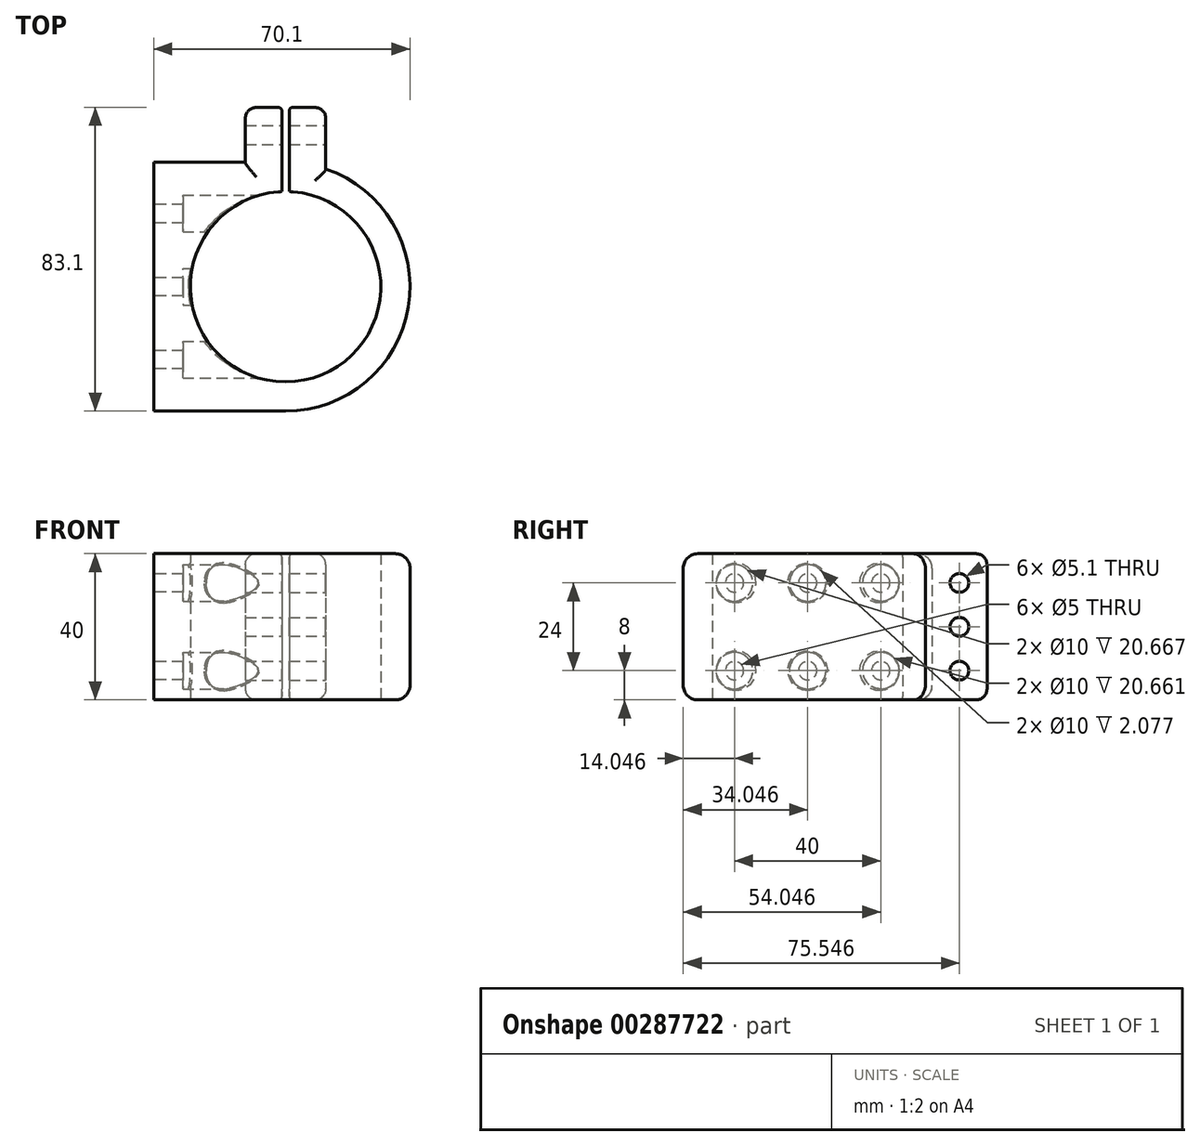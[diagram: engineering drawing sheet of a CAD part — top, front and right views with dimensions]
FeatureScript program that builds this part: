
annotation { "Feature Type Name" : "Feature", "Feature Type Description" : "" }
export const myFeature = defineFeature(function(context is Context, id is Id, definition is map)
    precondition{}
    {
        {
            var Q0;
            Q0=qCreatedBy(makeId("Top.planeOp"),FACE);
            var sketch = newSketch(context, id + "F0", { "sketchPlane" : qUnion([Q0])});
            skLineSegment(sketch, "E0.bottom", {"start": v(-43.2, -23.77) * mm, "end": v(-7.15, -23.77) * mm, "construction": true});
            skLineSegment(sketch, "E0.top", {"start": v(-43.2, 28.33) * mm, "end": v(-7.15, 28.33) * mm, "construction": true});
            skLineSegment(sketch, "E0.left", {"start": v(-43.2, -23.77) * mm, "end": v(-43.2, 28.33) * mm});
            skLineSegment(sketch, "E0.right", {"start": v(-7.15, -23.77) * mm, "end": v(-7.15, 28.33) * mm, "construction": true});
            skArc(sketch, "E1", {"start": v(-7.15, -23.77) * mm, "mid": v(18.9, 2.28) * mm, "end": v(-7.15, 28.33) * mm});
            skLineSegment(sketch, "E2", {"start": v(-43.2, -23.77) * mm, "end": v(-43.2, -31.77) * mm});
            skLineSegment(sketch, "E3", {"start": v(-43.2, -31.77) * mm, "end": v(-7.15, -31.77) * mm});
            skLineSegment(sketch, "E4", {"start": v(-43.2, 28.33) * mm, "end": v(-43.2, 36.33) * mm});
            skLineSegment(sketch, "E5", {"start": v(-43.2, 36.33) * mm, "end": v(-7.15, 36.33) * mm});
            skArc(sketch, "E6", {"start": v(-7.15, -31.77) * mm, "mid": v(26.9, 2.28) * mm, "end": v(-7.15, 36.33) * mm});
            skCircle(sketch, "E7", {"center": v(-7.15, 2.28) * mm, "radius": 26.05 * mm});
            skLineSegment(sketch, "E8", {"start": v(-18.15, 36.33) * mm, "end": v(-18.15, 51.33) * mm});
            skLineSegment(sketch, "E9", {"start": v(-8.15, 36.33) * mm, "end": v(-8.15, 51.33) * mm});
            skLineSegment(sketch, "E10", {"start": v(-8.15, 51.33) * mm, "end": v(-18.15, 51.33) * mm});
            skLineSegment(sketch, "E11", {"start": v(-6.15, 36.31) * mm, "end": v(-6.15, 51.33) * mm});
            skLineSegment(sketch, "E12", {"start": v(-6.15, 51.33) * mm, "end": v(3.85, 51.33) * mm});
            skLineSegment(sketch, "E13", {"start": v(3.85, 51.33) * mm, "end": v(3.85, 34.5) * mm});
            skLineSegment(sketch, "E14", {"start": v(-8.15, 36.33) * mm, "end": v(-8.15, 28.3) * mm});
            skLineSegment(sketch, "E15", {"start": v(-6.15, 36.31) * mm, "end": v(-6.15, 28.3) * mm});
            skSolve(sketch);
        }
        {
            var Q0;
            Q0=makeQuery(id+"F0.imprint","IMPRINT",FACE,{"disambiguationData":[TD([[makeQuery(id+"F0.imprint","IMPRINT",EDGE,{"derivedFrom":sQuery(id+"F0.wireOp",EDGE,"E0.left")}),-1.0]])]});
            var Q1;
            {var subQ0=sQuery(id+"F0.wireOp",EDGE,"E11");Q1=makeQuery(id+"F0.imprint","IMPRINT",FACE,{"disambiguationData":[TD([[makeQuery(id+"F0.imprint","IMPRINT",EDGE,{"derivedFrom":subQ0}),-1.0]])]});}
            var Q2;
            {var subQ0=sQuery(id+"F0.wireOp",EDGE,"E8");Q2=makeQuery(id+"F0.imprint","IMPRINT",FACE,{"disambiguationData":[TD([[makeQuery(id+"F0.imprint","IMPRINT",EDGE,{"derivedFrom":subQ0}),-1.0]])]});}
            extrude(context, id + "F1", {"entities" : qUnion([Q0, Q1, Q2]), "depth" : 40 * mm});
        }
        {
            var Q0;
            Q0=makeQuery(id+"F1.opExtrude","SWEPT_FACE",FACE,{"disambiguationData":[OSD([sQuery(id+"F0.wireOp",EDGE,"E13")])]});
            var sketch = newSketch(context, id + "F2", { "sketchPlane" : qUnion([Q0])});
            skCircle(sketch, "E16", {"center": v(43.78, 32) * mm, "radius": 2.55 * mm});
            skCircle(sketch, "E17", {"center": v(43.78, 20) * mm, "radius": 2.55 * mm});
            skCircle(sketch, "E18", {"center": v(43.78, 8) * mm, "radius": 2.55 * mm});
            skLineSegment(sketch, "E19", {"start": v(43.78, 32) * mm, "end": v(43.78, 20) * mm, "construction": true});
            skLineSegment(sketch, "E20", {"start": v(43.78, 20) * mm, "end": v(43.78, 8) * mm, "construction": true});
            skSolve(sketch);
        }
        {
            var Q0;
            Q0=makeQuery(id+"F2.imprint","IMPRINT",FACE,{"disambiguationData":[TD([[makeQuery(id+"F2.imprint","IMPRINT",EDGE,{"derivedFrom":sQuery(id+"F2.wireOp",EDGE,"E16")}),1.0]])]});
            var Q1;
            Q1=makeQuery(id+"F2.imprint","IMPRINT",FACE,{"disambiguationData":[TD([[makeQuery(id+"F2.imprint","IMPRINT",EDGE,{"derivedFrom":sQuery(id+"F2.wireOp",EDGE,"E17")}),1.0]])]});
            var Q2;
            Q2=makeQuery(id+"F2.imprint","IMPRINT",FACE,{"disambiguationData":[TD([[makeQuery(id+"F2.imprint","IMPRINT",EDGE,{"derivedFrom":sQuery(id+"F2.wireOp",EDGE,"E18")}),1.0]])]});
            extrude(context, id + "F3", {"entities" : qUnion([Q0, Q1, Q2]), "operationType" : NewBodyOperationType.REMOVE, "oppositeDirection" : true, "depth" : 25 * mm});
        }
        {
            var Q0;
            Q0=makeQuery(id+"F1.opExtrude","SWEPT_FACE",FACE,{"disambiguationData":[OSD([sQuery(id+"F0.wireOp",EDGE,"E0.left"),sQuery(id+"F0.wireOp",EDGE,"E2"),sQuery(id+"F0.wireOp",EDGE,"E4")])]});
            var sketch = newSketch(context, id + "F4", { "sketchPlane" : qUnion([Q0])});
            skCircle(sketch, "E21", {"center": v(-22.28, 32) * mm, "radius": 2.5 * mm});
            skCircle(sketch, "E22", {"center": v(17.72, 32) * mm, "radius": 2.5 * mm});
            skCircle(sketch, "E23", {"center": v(17.72, 8) * mm, "radius": 2.5 * mm});
            skCircle(sketch, "E24", {"center": v(-22.28, 8) * mm, "radius": 2.5 * mm});
            skLineSegment(sketch, "E25", {"start": v(-22.28, 32) * mm, "end": v(17.72, 32) * mm, "construction": true});
            skLineSegment(sketch, "E26", {"start": v(-2.28, 40) * mm, "end": v(-2.28, 32) * mm, "construction": true});
            skCircle(sketch, "E27", {"center": v(-2.28, 32) * mm, "radius": 2.5 * mm});
            skCircle(sketch, "E28", {"center": v(-2.28, 8) * mm, "radius": 2.5 * mm});
            skSolve(sketch);
        }
        {
            var Q0;
            Q0=makeQuery(id+"F4.imprint","IMPRINT",FACE,{"disambiguationData":[TD([[makeQuery(id+"F4.imprint","IMPRINT",EDGE,{"derivedFrom":sQuery(id+"F4.wireOp",EDGE,"E21")}),1.0]])]});
            var Q1;
            Q1=makeQuery(id+"F4.imprint","IMPRINT",FACE,{"disambiguationData":[TD([[makeQuery(id+"F4.imprint","IMPRINT",EDGE,{"derivedFrom":sQuery(id+"F4.wireOp",EDGE,"E22")}),1.0]])]});
            var Q2;
            Q2=makeQuery(id+"F4.imprint","IMPRINT",FACE,{"disambiguationData":[TD([[makeQuery(id+"F4.imprint","IMPRINT",EDGE,{"derivedFrom":sQuery(id+"F4.wireOp",EDGE,"E23")}),1.0]])]});
            var Q3;
            Q3=makeQuery(id+"F4.imprint","IMPRINT",FACE,{"disambiguationData":[TD([[makeQuery(id+"F4.imprint","IMPRINT",EDGE,{"derivedFrom":sQuery(id+"F4.wireOp",EDGE,"E24")}),1.0]])]});
            var Q4;
            Q4=makeQuery(id+"F4.imprint","IMPRINT",FACE,{"disambiguationData":[TD([[makeQuery(id+"F4.imprint","IMPRINT",EDGE,{"derivedFrom":sQuery(id+"F4.wireOp",EDGE,"E27")}),1.0]])]});
            var Q5;
            Q5=makeQuery(id+"F4.imprint","IMPRINT",FACE,{"disambiguationData":[TD([[makeQuery(id+"F4.imprint","IMPRINT",EDGE,{"derivedFrom":sQuery(id+"F4.wireOp",EDGE,"E28")}),1.0]])]});
            extrude(context, id + "F5", {"entities" : qUnion([Q0, Q1, Q2, Q3, Q4, Q5]), "operationType" : NewBodyOperationType.REMOVE, "oppositeDirection" : true, "depth" : 25 * mm});
        }
        {
            var Q0;
            Q0=makeQuery(id+"F1.opExtrude","SWEPT_FACE",FACE,{"disambiguationData":[OSD([sQuery(id+"F0.wireOp",EDGE,"E0.left"),sQuery(id+"F0.wireOp",EDGE,"E2"),sQuery(id+"F0.wireOp",EDGE,"E4")])]});
            cPlane(context, id + "F6", {"entities" : qUnion([Q0]), "cplaneType" : CPlaneType.OFFSET, "offset" : 30 * mm, "oppositeDirection" : true, "width" : 150 * mm, "height" : 150 * mm});
        }
        {
            var Q0;
            Q0=qCreatedBy(id+"F6.planeOp",FACE);
            var sketch = newSketch(context, id + "F7", { "sketchPlane" : qUnion([Q0])});
            skCircle(sketch, "E29.0", {"center": v(17.72, 32) * mm, "radius": 2.5 * mm});
            skCircle(sketch, "E30.0", {"center": v(-2.28, 32) * mm, "radius": 2.5 * mm});
            skCircle(sketch, "E31.0", {"center": v(-22.28, 32) * mm, "radius": 2.5 * mm});
            skCircle(sketch, "E32.0", {"center": v(-22.28, 8) * mm, "radius": 2.5 * mm});
            skCircle(sketch, "E33.0", {"center": v(-2.28, 8) * mm, "radius": 2.5 * mm});
            skCircle(sketch, "E34.0", {"center": v(17.72, 8) * mm, "radius": 2.5 * mm});
            skCircle(sketch, "E35", {"center": v(17.72, 32) * mm, "radius": 5 * mm});
            skCircle(sketch, "E36", {"center": v(-2.28, 32) * mm, "radius": 5 * mm});
            skCircle(sketch, "E37", {"center": v(-22.28, 32) * mm, "radius": 5 * mm});
            skCircle(sketch, "E38", {"center": v(-22.28, 8) * mm, "radius": 5 * mm});
            skCircle(sketch, "E39", {"center": v(-2.28, 8) * mm, "radius": 5 * mm});
            skCircle(sketch, "E40", {"center": v(17.72, 8) * mm, "radius": 5 * mm});
            skSolve(sketch);
        }
        {
            var Q0;
            Q0=makeQuery(id+"F7.imprint","IMPRINT",FACE,{"disambiguationData":[TD([[makeQuery(id+"F7.imprint","IMPRINT",EDGE,{"derivedFrom":sQuery(id+"F7.wireOp",EDGE,"E29.0")}),-1.0]])]});
            var Q1;
            Q1=makeQuery(id+"F7.imprint","IMPRINT",FACE,{"disambiguationData":[TD([[makeQuery(id+"F7.imprint","IMPRINT",EDGE,{"derivedFrom":sQuery(id+"F7.wireOp",EDGE,"E34.0")}),-1.0]])]});
            var Q2;
            Q2=makeQuery(id+"F7.imprint","IMPRINT",FACE,{"disambiguationData":[TD([[makeQuery(id+"F7.imprint","IMPRINT",EDGE,{"derivedFrom":sQuery(id+"F7.wireOp",EDGE,"E32.0")}),-1.0]])]});
            var Q3;
            Q3=makeQuery(id+"F7.imprint","IMPRINT",FACE,{"disambiguationData":[TD([[makeQuery(id+"F7.imprint","IMPRINT",EDGE,{"derivedFrom":sQuery(id+"F7.wireOp",EDGE,"E31.0")}),-1.0]])]});
            var Q4;
            Q4=makeQuery(id+"F7.imprint","IMPRINT",FACE,{"disambiguationData":[TD([[makeQuery(id+"F7.imprint","IMPRINT",EDGE,{"derivedFrom":sQuery(id+"F7.wireOp",EDGE,"E30.0")}),-1.0]])]});
            var Q5;
            Q5=makeQuery(id+"F7.imprint","IMPRINT",FACE,{"disambiguationData":[TD([[makeQuery(id+"F7.imprint","IMPRINT",EDGE,{"derivedFrom":sQuery(id+"F7.wireOp",EDGE,"E33.0")}),-1.0]])]});
            extrude(context, id + "F8", {"entities" : qUnion([Q0, Q1, Q2, Q3, Q4, Q5]), "operationType" : NewBodyOperationType.REMOVE, "depth" : 22 * mm});
        }
        {
            var Q0;
            Q0=makeQuery(id+"F1.opExtrude","CAP_EDGE",EDGE,{"disambiguationData":[OSD([sQuery(id+"F0.wireOp",EDGE,"E6")])],"isStart":false});
            var Q1;
            Q1=makeQuery(id+"F1.opExtrude","CAP_EDGE",EDGE,{"disambiguationData":[OSD([sQuery(id+"F0.wireOp",EDGE,"E6")])],"isStart":true});
            var Q2;
            Q2=makeQuery(id+"F1.opExtrude","CAP_EDGE",EDGE,{"disambiguationData":[OSD([sQuery(id+"F0.wireOp",EDGE,"E5")])],"isStart":true});
            var Q3;
            Q3=makeQuery(id+"F1.opExtrude","CAP_EDGE",EDGE,{"disambiguationData":[OSD([sQuery(id+"F0.wireOp",EDGE,"E5")])],"isStart":false});
            fillet(context, id + "F9", {"entities" : qUnion([Q0, Q1, Q2, Q3]), "radius" : 4 * mm, "tangentPropagation" : true, "allowEdgeOverflow" : false});
        }
        {
            var Q0;
            Q0=makeQuery(id+"F8.boolean.opBoolean","INTERSECT",EDGE,{"derivedFrom":[makeQuery(id+"F1.opExtrude","SWEPT_FACE",FACE,{"disambiguationData":[OSD([sQuery(id+"F0.wireOp",EDGE,"E7")])]}),makeQuery(id+"F8.opExtrude","SWEPT_FACE",FACE,{"disambiguationData":[OSD([sQuery(id+"F7.wireOp",EDGE,"E40")])]})]});
            var Q1;
            Q1=makeQuery(id+"F8.boolean.opBoolean","INTERSECT",EDGE,{"derivedFrom":[makeQuery(id+"F1.opExtrude","SWEPT_FACE",FACE,{"disambiguationData":[OSD([sQuery(id+"F0.wireOp",EDGE,"E7")])]}),makeQuery(id+"F8.opExtrude","SWEPT_FACE",FACE,{"disambiguationData":[OSD([sQuery(id+"F7.wireOp",EDGE,"E35")])]})]});
            var Q2;
            Q2=makeQuery(id+"F8.boolean.opBoolean","INTERSECT",EDGE,{"derivedFrom":[makeQuery(id+"F1.opExtrude","SWEPT_FACE",FACE,{"disambiguationData":[OSD([sQuery(id+"F0.wireOp",EDGE,"E7")])]}),makeQuery(id+"F8.opExtrude","SWEPT_FACE",FACE,{"disambiguationData":[OSD([sQuery(id+"F7.wireOp",EDGE,"E39")])]})]});
            var Q3;
            Q3=makeQuery(id+"F8.boolean.opBoolean","INTERSECT",EDGE,{"derivedFrom":[makeQuery(id+"F1.opExtrude","SWEPT_FACE",FACE,{"disambiguationData":[OSD([sQuery(id+"F0.wireOp",EDGE,"E7")])]}),makeQuery(id+"F8.opExtrude","SWEPT_FACE",FACE,{"disambiguationData":[OSD([sQuery(id+"F7.wireOp",EDGE,"E36")])]})]});
            var Q4;
            Q4=makeQuery(id+"F8.boolean.opBoolean","INTERSECT",EDGE,{"derivedFrom":[makeQuery(id+"F1.opExtrude","SWEPT_FACE",FACE,{"disambiguationData":[OSD([sQuery(id+"F0.wireOp",EDGE,"E7")])]}),makeQuery(id+"F8.opExtrude","SWEPT_FACE",FACE,{"disambiguationData":[OSD([sQuery(id+"F7.wireOp",EDGE,"E38")])]})]});
            var Q5;
            Q5=makeQuery(id+"F8.boolean.opBoolean","INTERSECT",EDGE,{"derivedFrom":[makeQuery(id+"F1.opExtrude","SWEPT_FACE",FACE,{"disambiguationData":[OSD([sQuery(id+"F0.wireOp",EDGE,"E7")])]}),makeQuery(id+"F8.opExtrude","SWEPT_FACE",FACE,{"disambiguationData":[OSD([sQuery(id+"F7.wireOp",EDGE,"E37")])]})]});
            fillet(context, id + "F10", {"entities" : qUnion([Q0, Q1, Q2, Q3, Q4, Q5]), "radius" : 0.5 * mm, "tangentPropagation" : true, "allowEdgeOverflow" : false});
        }
        {
            var Q0;
            Q0=makeQuery(id+"F1.opExtrude","CAP_EDGE",EDGE,{"disambiguationData":[OSD([sQuery(id+"F0.wireOp",EDGE,"E8")])],"isStart":true});
            var Q1;
            Q1=makeQuery(id+"F1.opExtrude","SWEPT_EDGE",EDGE,{"disambiguationData":[OSD([sQuery(id+"F0.wireOp",EDGE,"E8"),sQuery(id+"F0.wireOp",EDGE,"E10")])]});
            var Q2;
            Q2=makeQuery(id+"F1.opExtrude","CAP_EDGE",EDGE,{"disambiguationData":[OSD([sQuery(id+"F0.wireOp",EDGE,"E8")])],"isStart":false});
            var Q3;
            Q3=makeQuery(id+"F1.opExtrude","CAP_EDGE",EDGE,{"disambiguationData":[OSD([sQuery(id+"F0.wireOp",EDGE,"E10")])],"isStart":false});
            var Q4;
            Q4=makeQuery(id+"F1.opExtrude","CAP_EDGE",EDGE,{"disambiguationData":[OSD([sQuery(id+"F0.wireOp",EDGE,"E10")])],"isStart":true});
            var Q5;
            Q5=makeQuery(id+"F1.opExtrude","CAP_EDGE",EDGE,{"disambiguationData":[OSD([sQuery(id+"F0.wireOp",EDGE,"E12")])],"isStart":true});
            var Q6;
            Q6=makeQuery(id+"F1.opExtrude","CAP_EDGE",EDGE,{"disambiguationData":[OSD([sQuery(id+"F0.wireOp",EDGE,"E12")])],"isStart":false});
            var Q7;
            Q7=makeQuery(id+"F1.opExtrude","SWEPT_EDGE",EDGE,{"disambiguationData":[OSD([sQuery(id+"F0.wireOp",EDGE,"E12"),sQuery(id+"F0.wireOp",EDGE,"E13")])]});
            var Q8;
            Q8=makeQuery(id+"F1.opExtrude","CAP_EDGE",EDGE,{"disambiguationData":[OSD([sQuery(id+"F0.wireOp",EDGE,"E13")])],"isStart":true});
            var Q9;
            Q9=makeQuery(id+"F1.opExtrude","CAP_EDGE",EDGE,{"disambiguationData":[OSD([sQuery(id+"F0.wireOp",EDGE,"E13")])],"isStart":false});
            fillet(context, id + "F11", {"entities" : qUnion([Q0, Q1, Q2, Q3, Q4, Q5, Q6, Q7, Q8, Q9]), "radius" : 3 * mm, "tangentPropagation" : true, "allowEdgeOverflow" : false});
        }
        {
            var Q0;
            Q0=makeQuery(id+"F1.opExtrude","CAP_EDGE",EDGE,{"disambiguationData":[OSD([sQuery(id+"F0.wireOp",EDGE,"E9"),sQuery(id+"F0.wireOp",EDGE,"E14")])],"isStart":true});
            var Q1;
            Q1=makeQuery(id+"F1.opExtrude","CAP_EDGE",EDGE,{"disambiguationData":[OSD([sQuery(id+"F0.wireOp",EDGE,"E11"),sQuery(id+"F0.wireOp",EDGE,"E15")])],"isStart":true});
            var Q2;
            Q2=makeQuery(id+"F1.opExtrude","SWEPT_EDGE",EDGE,{"disambiguationData":[OSD([sQuery(id+"F0.wireOp",EDGE,"E11"),sQuery(id+"F0.wireOp",EDGE,"E12")])]});
            var Q3;
            Q3=makeQuery(id+"F1.opExtrude","SWEPT_EDGE",EDGE,{"disambiguationData":[OSD([sQuery(id+"F0.wireOp",EDGE,"E9"),sQuery(id+"F0.wireOp",EDGE,"E10")])]});
            fillet(context, id + "F12", {"entities" : qUnion([Q0, Q1, Q2, Q3]), "radius" : 1 * mm, "tangentPropagation" : true, "allowEdgeOverflow" : false});
        }
    });
